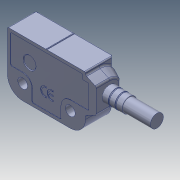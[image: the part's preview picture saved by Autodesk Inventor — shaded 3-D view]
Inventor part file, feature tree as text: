
AUTODESK INVENTOR PART (.ipt)
format: ipt  version: 2020.3 (Build 243373000, 373)  size: 1,149,440 bytes
history: native  units: in
note: dims shown in document units (in); Inventor stores cm internally (conversion verified against a paired STEP export)
features: other x5, extrude x1, sketch x1
ambient origin geometry x8: Origin, YZ Plane, XZ Plane, XY Plane, X Axis, Y Axis, Z Axis, Center Point
bodies: Solid1 (feature_tree), Solid2 (feature_tree), Solid3 (feature_tree), Solid4 (feature_tree), Solid5 (feature_tree)
feature tree (7):
  extrude  "Extrusion1"  Depth=1.0in TaperAngle=0.0deg
  sketch  "Sketch1"  dims[d0=0.5in d1=1.0in d2=0.0in]
  other  "Switch Box Right MP (Iss2)-1-solid1"
  other  "Sealing Plug (Iss4)-2-solid1"
  other  "Grommet (Iss3)-1-solid1"
  other  "Switch Lid Right MP (JOB-1362)-1-solid1"
  other  "Cut-Extrude1"
